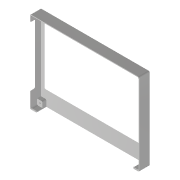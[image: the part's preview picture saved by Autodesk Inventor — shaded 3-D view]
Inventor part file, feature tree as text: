
AUTODESK INVENTOR PART (.ipt)
format: ipt  version: 2022 (Build 260153000, 153)  size: 256,000 bytes
history: native  units: mm
features: other x5, sketch x2, extrude x2, reference x2, pattern_linear x1
ambient origin geometry x8: Origin, YZ Plane, XZ Plane, XY Plane, X Axis, Y Axis, Z Axis, Center Point
bodies: Volumenkörper1 (feature_tree)
feature tree (12):
  other  "40_ZTable_7Inch_Display_Housing_Lid"
  sketch  "Skizze1"  dims[d0=3.2mm d1=10.0mm]
  other  "Arbeitspunkt1"
  extrude  "Extrusion1"  Depth=10.0mm
  extrude  "Extrusion2"  Depth=4.0mm
  pattern_linear  "Rechteckige Anordnung1"  Spacing1=169.0mm  [1 undecoded]
  reference  "Referenz1"
  reference  "Referenz2"
  sketch  "Skizze2"  dims[d3=5.0mm d4=4.0mm d5=169.0mm d6=0.0mm d7=25.0mm d8=169.0mm d9=0.0mm d10=50.0mm d12=40.0mm]
  other  "MeshFeature1"
  other  "Assembly_7inch_Display.iam"
  other  "40_ZTable_7Inch_Display_Housing_Bottom:1"
note: 1 required parameter value undecoded (feature->parameter linkage not recoverable at this tier; creation-order binding heuristic only, values carry confidence <= 0.55)
